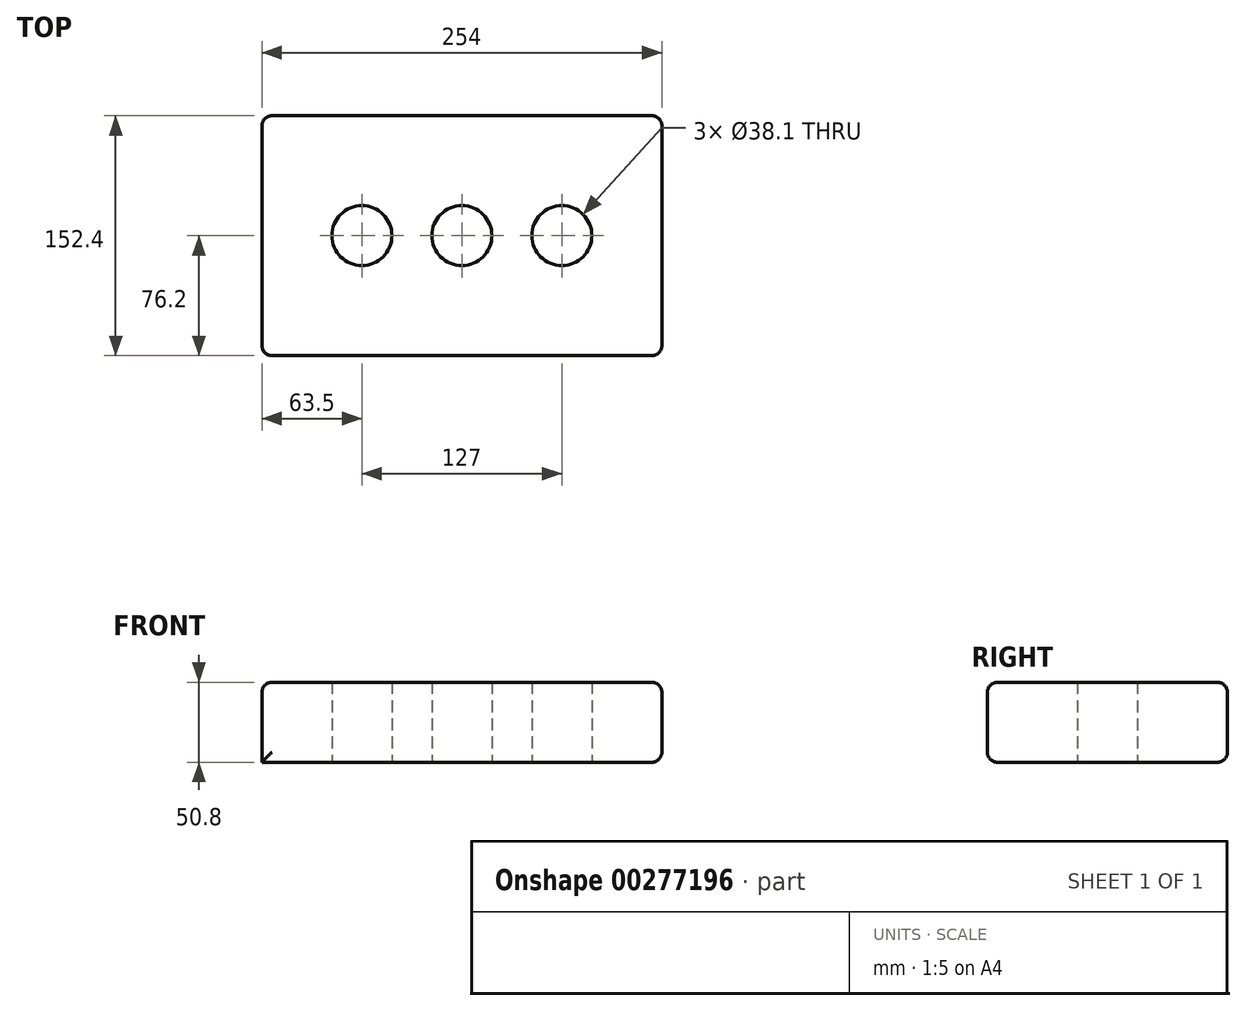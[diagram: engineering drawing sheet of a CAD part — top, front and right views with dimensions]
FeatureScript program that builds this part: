
annotation { "Feature Type Name" : "Feature", "Feature Type Description" : "" }
export const myFeature = defineFeature(function(context is Context, id is Id, definition is map)
    precondition{}
    {
        {
            var Q0;
            Q0=qCreatedBy(makeId("Top.planeOp"),FACE);
            var sketch = newSketch(context, id + "F0", { "sketchPlane" : qUnion([Q0])});
            skLineSegment(sketch, "E0.bottom", {"start": v(127, 76.2) * mm, "end": v(-127, 76.2) * mm});
            skLineSegment(sketch, "E0.top", {"start": v(127, -76.2) * mm, "end": v(-127, -76.2) * mm});
            skLineSegment(sketch, "E0.left", {"start": v(127, 76.2) * mm, "end": v(127, -76.2) * mm});
            skLineSegment(sketch, "E0.right", {"start": v(-127, 76.2) * mm, "end": v(-127, -76.2) * mm});
            skPoint(sketch, "E0.middle", {"position": v(0, 0) * mm});
            skCircle(sketch, "E1", {"center": v(0, 0) * mm, "radius": 19.05 * mm});
            skCircle(sketch, "E2", {"center": v(63.5, 0) * mm, "radius": 19.05 * mm});
            skCircle(sketch, "E3", {"center": v(-63.5, 0) * mm, "radius": 19.05 * mm});
            skSolve(sketch);
        }
        {
            var Q0;
            Q0 = qSketchRegion(id + "F0", true);
            extrude(context, id + "F1", {"entities" : qUnion([Q0]), "depth" : 50.8 * mm});
        }
        {
            var Q0;
            Q0=makeQuery(id+"F1.opExtrude","CAP_EDGE",EDGE,{"disambiguationData":[OSD([sQuery(id+"F0.wireOp",EDGE,"E0.top")])],"isStart":false});
            var Q1;
            Q1=makeQuery(id+"F1.opExtrude","CAP_EDGE",EDGE,{"disambiguationData":[OSD([sQuery(id+"F0.wireOp",EDGE,"E0.right")])],"isStart":false});
            var Q2;
            Q2=makeQuery(id+"F1.opExtrude","CAP_EDGE",EDGE,{"disambiguationData":[OSD([sQuery(id+"F0.wireOp",EDGE,"E0.left")])],"isStart":true});
            var Q3;
            Q3=makeQuery(id+"F1.opExtrude","CAP_EDGE",EDGE,{"disambiguationData":[OSD([sQuery(id+"F0.wireOp",EDGE,"E0.left")])],"isStart":false});
            var Q4;
            Q4=makeQuery(id+"F1.opExtrude","SWEPT_FACE",FACE,{"disambiguationData":[OSD([sQuery(id+"F0.wireOp",EDGE,"E0.top")])]});
            var Q5;
            Q5=makeQuery(id+"F1.opExtrude","SWEPT_FACE",FACE,{"disambiguationData":[OSD([sQuery(id+"F0.wireOp",EDGE,"E0.bottom")])]});
            fillet(context, id + "F2", {"entities" : qUnion([Q0, Q1, Q2, Q3, Q4, Q5]), "radius" : 6.35 * mm, "tangentPropagation" : true, "allowEdgeOverflow" : false});
        }
    });
